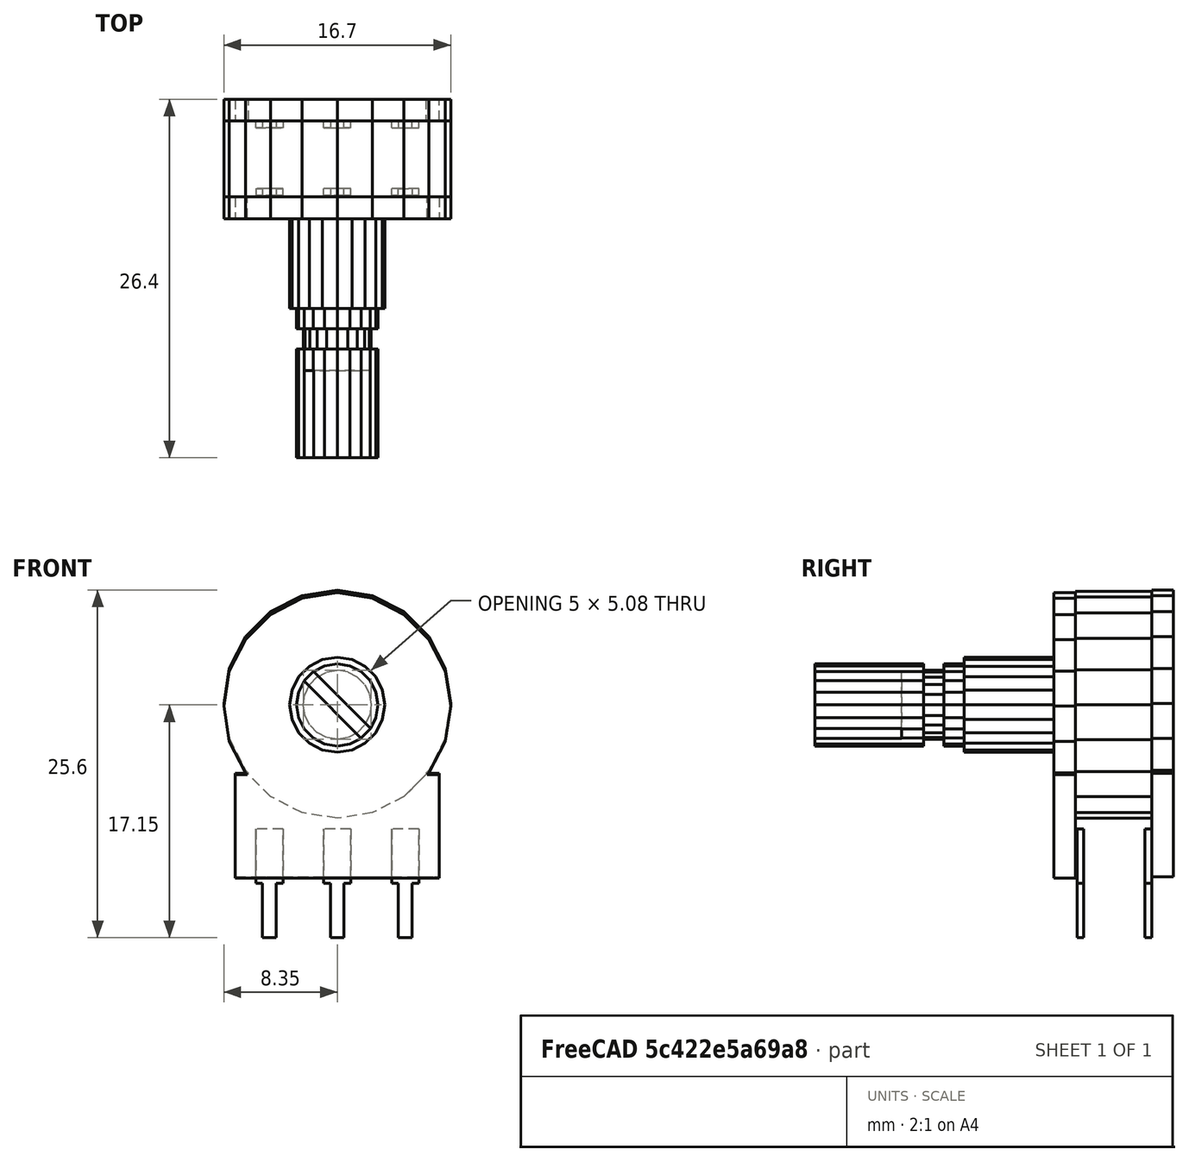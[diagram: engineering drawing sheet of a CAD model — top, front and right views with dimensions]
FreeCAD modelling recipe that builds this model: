
FCSTD DOCUMENT  (FreeCAD 0.19R24276 (Git))
Label: VRX2
License: All rights reserved
LicenseURL: http://en.wikipedia.org/wiki/All_rights_reserved
objects: Mesh::Feature×5, Part::Feature×5, Part::Refine×5, Part::FeaturePython×1
note: 11 computed .brp shape members not serialized (recipe doc carries the construction recipe); baked Part::Feature solids carry a one-line shape summary decoded from their .brp

FEATURE [Mesh::Feature] VR_X_2__1_  label="VR X 2 (1)"
FEATURE [Mesh::Feature] VR_X_2__2_  label="VR X 2 (2)"
FEATURE [Mesh::Feature] VR_X_2__3_  label="VR X 2 (3)"
FEATURE [Mesh::Feature] VR_X_2__4_  label="VR X 2 (4)"
FEATURE [Mesh::Feature] VR_X_2  label="VR X 2"
FEATURE [Part::Feature] VR_X_2__1_001
  shape: bbox 16.7 x 8.8 x 21.2 mm, 160 faces, 0 solids (baked)
FEATURE [Part::Feature] VR_X_2__2_001
  shape: bbox 16.7 x 5.6 x 16.7 mm, 76 faces, 0 solids (baked)
FEATURE [Part::Feature] VR_X_2__3_001
  shape: bbox 7 x 6.6 x 7 mm, 76 faces, 0 solids (baked)
FEATURE [Part::Feature] VR_X_2__4_001
  shape: bbox 6 x 11 x 6.05 mm, 256 faces, 0 solids (baked)
FEATURE [Part::Feature] VR_X_2001
  shape: bbox 12 x 5.5 x 8 mm, 168 faces, 0 solids (baked)
FEATURE [Part::Refine] VR_X_2__1_001001
  Source = -> VR_X_2__1_001
FEATURE [Part::Refine] VR_X_2__2_001001
  Source = -> VR_X_2__2_001
FEATURE [Part::Refine] VR_X_2__3_001001
  Source = -> VR_X_2__3_001
FEATURE [Part::Refine] VR_X_2__4_001001
  Source = -> VR_X_2__4_001
FEATURE [Part::Refine] VR_X_2001001
  Source = -> VR_X_2001
FEATURE [Part::FeaturePython] Connect  # WARN: FeaturePython — macro-defined, semantics opaque (R4)
  Objects = -> [VR_X_2__1_001001,VR_X_2__2_001001,VR_X_2__3_001001,VR_X_2__4_001001,VR_X_2001001]
  Tolerance = 0
